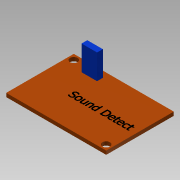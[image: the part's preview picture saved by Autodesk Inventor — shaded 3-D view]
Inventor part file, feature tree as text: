
AUTODESK INVENTOR PART (.ipt)
format: ipt  version: 2015 SP1 (Build 190203100, 203)  size: 99,328 bytes
history: native  units: mm
features: sketch x3, extrude x2
ambient origin geometry x8: Origin, YZ Plane, XZ Plane, XY Plane, X Axis, Y Axis, Z Axis, Center Point
bodies: Solid1 (feature_tree)
feature tree (5):
  sketch  "Sketch1"  dims[d0=46.5mm d1=31.42mm]
  extrude  "Extrusion1"  Depth=31.42mm
  extrude  "Extrusion2"  Depth=3.5mm
  sketch  "Sketch2"  dims[d2=3.5mm d3=3.5mm]
  sketch  "Sketch3"  dims[d4=2.5mm d5=2.5mm d6=2.5mm d7=2.5mm d8=1.7mm d9=0.0mm d10=13.25mm d11=0.0mm]
